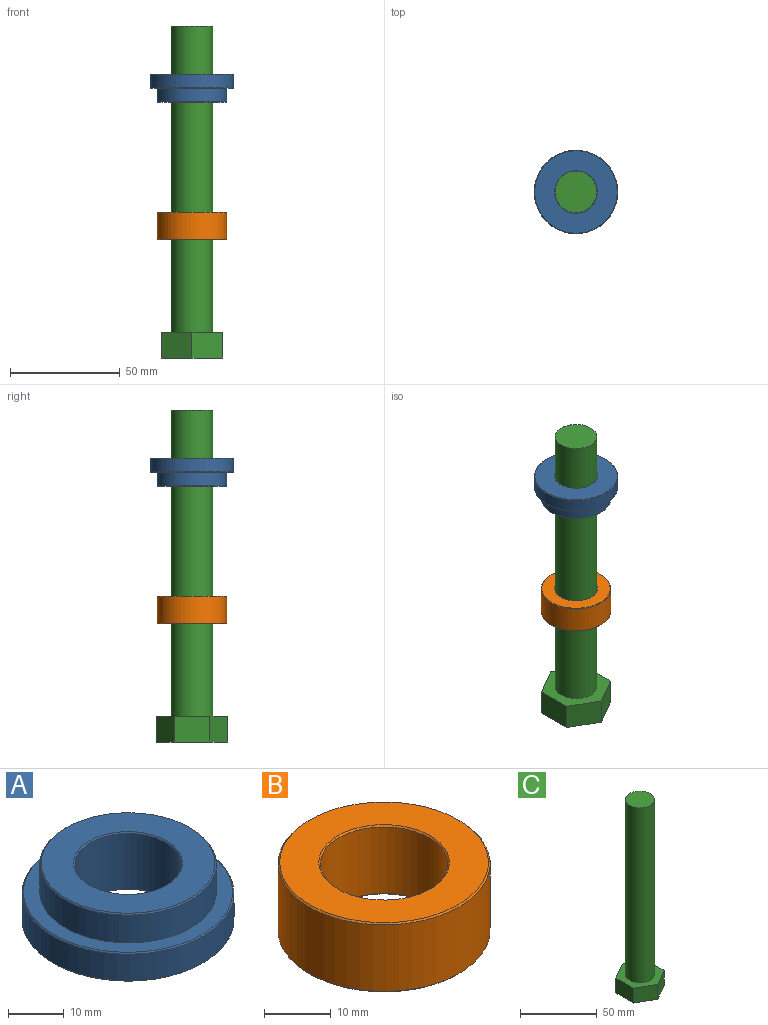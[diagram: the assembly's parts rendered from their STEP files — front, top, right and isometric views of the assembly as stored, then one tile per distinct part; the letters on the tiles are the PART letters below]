
ASSEMBLY  parts=3 mates=2
PART A: 11 faces, bbox 38.1x38.1x12.7 mm
  f0: cylinder r=9.53mm len=19.05mm, axis (0,0,-1), area 729.7mm2, adj f8,f10
  f1: cylinder r=19.05mm len=38.1mm, axis (0,0,-1), area 699.3mm2, adj f6,f9
  f2: plane 37.59x37.59mm, normal (0,0,1), area 318.2mm2, adj f4,f6
  f3: plane 37.59x37.59mm, normal (0,0,-1), area 809.5mm2, adj f9,f10
  f4: cylinder r=15.88mm len=31.75mm, axis (0,0,-1), area 608mm2, adj f2,f7
  f5: plane 31.24x31.24mm, normal (0,0,1), area 466.2mm2, adj f7,f8
  f6: cone r=18.8mm half-angle=45deg, axis (0,0,-1), area 42.7mm2, adj f1,f2
  f7: cone r=15.62mm half-angle=45deg, axis (0,0,-1), area 35.5mm2, adj f4,f5
  f8: cone r=9.53mm half-angle=45deg, axis (0,0,1), area 21.8mm2, adj f0,f5
  f9: cone r=19.05mm half-angle=45deg, axis (0,0,1), area 42.7mm2, adj f1,f3
  f10: cone r=9.78mm half-angle=45deg, axis (0,0,-1), area 21.8mm2, adj f0,f3
PART B: 8 faces, bbox 31.8x31.8x12.7 mm
  f0: cylinder r=9.53mm len=19.05mm, axis (0,0,-1), area 729.7mm2, adj f6,f7
  f1: cylinder r=15.88mm len=31.75mm, axis (0,0,-1), area 1216.1mm2, adj f4,f5
  f2: plane 31.24x31.24mm, normal (0,0,1), area 466.2mm2, adj f4,f6
  f3: plane 31.24x31.24mm, normal (0,0,-1), area 466.2mm2, adj f5,f7
  f4: cone r=15.62mm half-angle=45deg, axis (0,0,-1), area 35.5mm2, adj f1,f2
  f5: cone r=15.88mm half-angle=45deg, axis (0,0,1), area 35.5mm2, adj f1,f3
  f6: cone r=9.53mm half-angle=45deg, axis (0,0,1), area 21.8mm2, adj f0,f2
  f7: cone r=9.78mm half-angle=45deg, axis (0,0,-1), area 21.8mm2, adj f0,f3
PART C: 10 faces, bbox 28.2x32.6x151.5 mm
  f0: cylinder r=9.53mm len=139.7mm, axis (0,0,-1), area 8360.7mm2, adj f1,f9
  f1: plane 19.05x19.05mm, normal (0,0,1), area 285mm2, adj f0
  f2: plane 16.28x11.81mm, normal (1,0,0), area 192.3mm2, adj f3,f7,f8,f9
  f3: plane 14.1x11.81mm, normal (0.5,0.87,0), area 192.3mm2, adj f2,f4,f8,f9
  f4: plane 14.1x11.81mm, normal (-0.5,0.87,0), area 192.3mm2, adj f3,f5,f8,f9
  f5: plane 16.28x11.81mm, normal (-1,0,0), area 192.3mm2, adj f4,f6,f8,f9
  f6: plane 14.1x11.81mm, normal (-0.5,-0.87,0), area 192.3mm2, adj f5,f7,f8,f9
  f7: plane 14.1x11.81mm, normal (0.5,-0.87,0), area 192.3mm2, adj f2,f6,f8,f9
  f8: plane 32.56x28.19mm, normal (0,0,-1), area 688.4mm2, adj f2,f3,f4,f5,f6,f7
  f9: plane 32.56x28.19mm, normal (0,0,1), area 403.4mm2, adj f0,f2,f3,f4,f5,f6,f7
PLACE A rot(axis=(1,0,0),180deg) t=(17.13,27.05,107.8)mm
PLACE B t=(17.13,27.05,32.17)mm
PLACE C t=(17.13,27.05,-9.89)mm
MATE cylindrical A.f0 <-> C.f0  axis (0,0,1) through (17.13,27.05,95.35)mm
MATE cylindrical B.f1 <-> C.f0  axis (0,0,-1) through (17.13,27.05,44.61)mm
